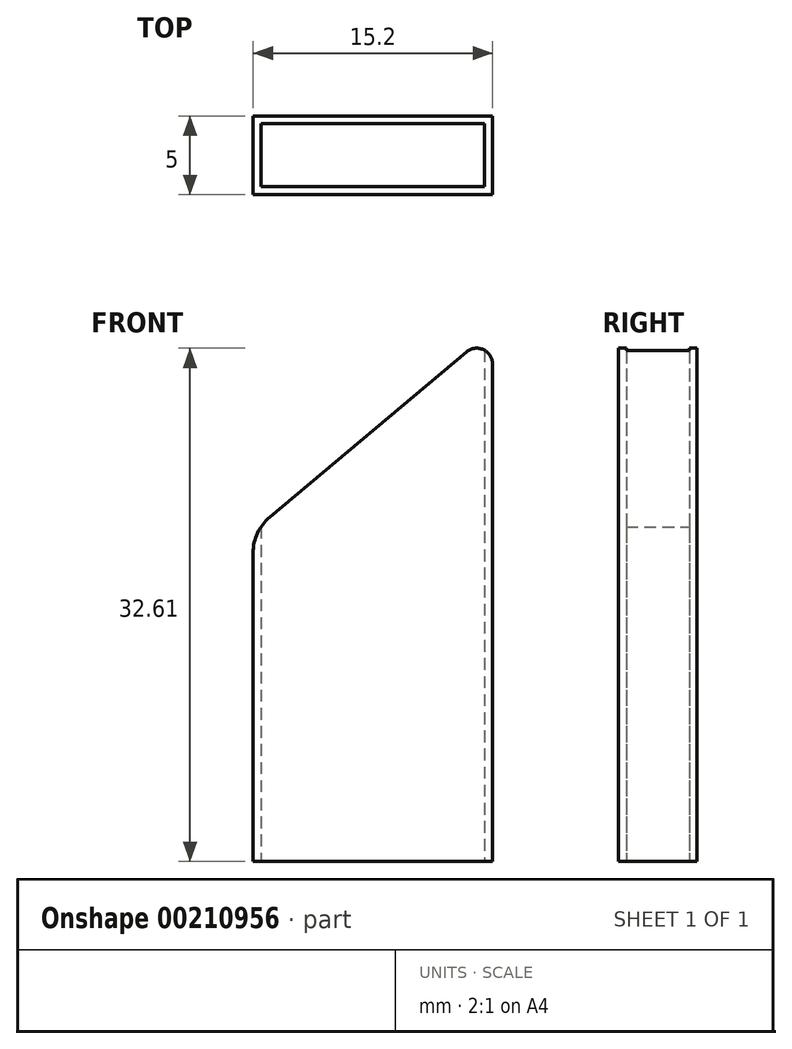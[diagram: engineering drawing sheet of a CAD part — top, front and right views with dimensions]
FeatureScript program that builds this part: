
annotation { "Feature Type Name" : "Feature", "Feature Type Description" : "" }
export const myFeature = defineFeature(function(context is Context, id is Id, definition is map)
    precondition{}
    {
        {
            var Q0;
            Q0=qCreatedBy(makeId("Top.planeOp"),FACE);
            var sketch = newSketch(context, id + "F0", { "sketchPlane" : qUnion([Q0])});
            skLineSegment(sketch, "E0.bottom", {"start": v(7.1, -2) * mm, "end": v(-7.1, -2) * mm});
            skLineSegment(sketch, "E0.top", {"start": v(7.1, 2) * mm, "end": v(-7.1, 2) * mm});
            skLineSegment(sketch, "E0.left", {"start": v(7.1, -2) * mm, "end": v(7.1, 2) * mm});
            skLineSegment(sketch, "E0.right", {"start": v(-7.1, -2) * mm, "end": v(-7.1, 2) * mm});
            skPoint(sketch, "E0.middle", {"position": v(0, 0) * mm});
            skLineSegment(sketch, "E1.bottom", {"start": v(7.6, -2.5) * mm, "end": v(-7.6, -2.5) * mm});
            skLineSegment(sketch, "E1.top", {"start": v(7.6, 2.5) * mm, "end": v(-7.6, 2.5) * mm});
            skLineSegment(sketch, "E1.left", {"start": v(7.6, -2.5) * mm, "end": v(7.6, 2.5) * mm});
            skLineSegment(sketch, "E1.right", {"start": v(-7.6, -2.5) * mm, "end": v(-7.6, 2.5) * mm});
            skSolve(sketch);
        }
        {
            var Q0;
            Q0=qSketchRegion(id+"F0",true);
            extrude(context, id + "F1", {"entities" : qUnion([Q0]), "depth" : 21 * mm});
        }
        {
            var Q0;
            Q0=makeQuery(id+"F1.opExtrude","CAP_EDGE",EDGE,{"disambiguationData":[OSD([sQuery(id+"F0.wireOp",EDGE,"E1.right")])],"isStart":false});
            var Q1;
            Q1=makeQuery(id+"F1.opExtrude","CAP_FACE",FACE,{"disambiguationData":[OSD([sQuery(id+"F0.wireOp",EDGE,"E0.bottom"),sQuery(id+"F0.wireOp",EDGE,"E0.top"),sQuery(id+"F0.wireOp",EDGE,"E0.left"),sQuery(id+"F0.wireOp",EDGE,"E0.right"),sQuery(id+"F0.wireOp",EDGE,"E1.bottom"),sQuery(id+"F0.wireOp",EDGE,"E1.top"),sQuery(id+"F0.wireOp",EDGE,"E1.left"),sQuery(id+"F0.wireOp",EDGE,"E1.right")])],"isStart":false});
            cPlane(context, id + "F2", {"entities" : qUnion([Q0, Q1]), "cplaneType" : CPlaneType.LINE_ANGLE, "offset" : 25 * mm, "angle" : 140 * degree, "width" : 150 * mm, "height" : 150 * mm});
        }
        {
            var Q0;
            Q0=makeQuery(id+"F1.opExtrude","CAP_FACE",FACE,{"disambiguationData":[OSD([sQuery(id+"F0.wireOp",EDGE,"E0.bottom"),sQuery(id+"F0.wireOp",EDGE,"E0.top"),sQuery(id+"F0.wireOp",EDGE,"E0.left"),sQuery(id+"F0.wireOp",EDGE,"E0.right"),sQuery(id+"F0.wireOp",EDGE,"E1.bottom"),sQuery(id+"F0.wireOp",EDGE,"E1.top"),sQuery(id+"F0.wireOp",EDGE,"E1.left"),sQuery(id+"F0.wireOp",EDGE,"E1.right")])],"isStart":false});
            var sketch = newSketch(context, id + "F3", { "sketchPlane" : qUnion([Q0])});
            skLineSegment(sketch, "E2", {"start": v(-7.1, 2) * mm, "end": v(-7.1, -2) * mm});
            skLineSegment(sketch, "E3", {"start": v(-7.1, -2) * mm, "end": v(7.1, -2) * mm});
            skLineSegment(sketch, "E4", {"start": v(7.1, -2) * mm, "end": v(7.1, 2) * mm});
            skLineSegment(sketch, "E5", {"start": v(7.1, 2) * mm, "end": v(-7.1, 2) * mm});
            skLineSegment(sketch, "E6", {"start": v(-7.6, 2.5) * mm, "end": v(-7.6, -2.5) * mm});
            skLineSegment(sketch, "E7", {"start": v(-7.6, -2.5) * mm, "end": v(7.6, -2.5) * mm});
            skLineSegment(sketch, "E8", {"start": v(7.6, -2.5) * mm, "end": v(7.6, 2.5) * mm});
            skLineSegment(sketch, "E9", {"start": v(7.6, 2.5) * mm, "end": v(-7.6, 2.5) * mm});
            skSolve(sketch);
        }
        {
            var Q0;
            Q0=qSketchRegion(id+"F3",true);
            var Q1;
            Q1=qCreatedBy(id+"F2.planeOp",FACE);
            extrude(context, id + "F4", {"entities" : qUnion([Q0]), "operationType" : NewBodyOperationType.ADD, "endBound" : BoundingType.UP_TO_SURFACE, "endBoundEntityFace" : qUnion([Q1]), "depth" : 25 * mm});
        }
        {
            var Q0;
            Q0=makeQuery(id+"F4.opExtrude","CAP_EDGE",EDGE,{"disambiguationData":[OSD([sQuery(id+"F3.wireOp",EDGE,"E8")])],"isStart":false});
            fillet(context, id + "F5", {"entities" : qUnion([Q0]), "radius" : 1 * mm, "tangentPropagation" : true, "allowEdgeOverflow" : false});
        }
        {
            var Q0;
            Q0=makeQuery(id+"F4.boolean.opBoolean","MERGE",EDGE,{"derivedFrom":[makeQuery(id+"F1.opExtrude","CAP_EDGE",EDGE,{"disambiguationData":[OSD([sQuery(id+"F0.wireOp",EDGE,"E1.right")])],"isStart":false}),makeQuery(id+"F4.opExtrude","CAP_EDGE",EDGE,{"disambiguationData":[OSD([sQuery(id+"F3.wireOp",EDGE,"E6")])],"isStart":false})]});
            fillet(context, id + "F6", {"entities" : qUnion([Q0]), "radius" : 3 * mm, "tangentPropagation" : true, "allowEdgeOverflow" : false});
        }
    });
